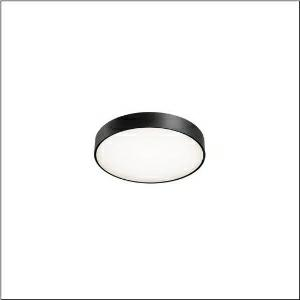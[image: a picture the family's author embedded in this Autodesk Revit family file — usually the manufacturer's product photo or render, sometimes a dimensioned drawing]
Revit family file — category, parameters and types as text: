
# Revit family: round_21_s_51mr34fd0421b
name_source: partatom
category: Lighting Fixtures
units: mm (PartAtom-declared; Revit-internal decimal feet)

## family parameters
Cut with Voids When Loaded = No
Host = Face
Light Source = No
Part Type = Normal
Room Calculation Point = No
Round Connector Dimension = Use Diameter
Shared = No

## types (1)
- Round 21 S (1 x LED, 3910 lm, 30.3 W, 4000K)
    Apparent Load = 30 VA
    CIE Flux Codes = 49 80 96 100 100
    Color Rendering = 80
    Color Temperature = 4000K
    Default Elevation = 1800 mm
    Description = Round 21 S, wall and ceiling luminaire, primary optical cover: cover, of PMMA, opal, light emission: direct distribution, primary light characteristic: symmetric, installation type: suspended mounting, surface-mounted, LED, rated luminous flux: 3.900lm, luminous efficacy: 129lm/W, light colour: 840, colour temperature: 4000K, control gear: DALI 2, with terminal, 5-pole, mains connection: 230V, AC, 50/60Hz, rated input power: 30.3W, housing, of aluminium, coated, black, diameter: 400mm, height: 62mm, protection rating (complete): IP40, insulation class (complete): insulation class I (protective earthing), certification: CE, impact resistance: IK04, permissible operating ambient temperature: -10..+35°C, packaging unit: 1 piece
    Height = 87 mm
    Lamp = 1 x LED
    Lamp Light Flux = 3910 lm
    Lamp Power = 30.3 W
    Lamp count = 1
    Length = 400 mm
    Luminous efficacy = 129 lm/W
    Manufacturer = Siteco
    ModVariant = No
    Model = 51MR34FD0421B
    Mounting Place = Ceiling
    Mounting Type = Surface mounted
    Number of Poles = 1
    OnlyDefault = Yes
    Power Factor = 1
    Product Name = Round 21 S
    Product group = wall and ceiling luminaire | ceiling mounted
    ProductGroupID = 304
    Protection Class = Protection class I
    Protection Degree = IP 40
    RLX_Detail_Level = 1
    RLX_Emergency_Light_Flux = 0 lm
    RLX_Emergency_Type = 0
    RLX_Emergency_Type_DB = No
    RlxData = <blob elided: 13461 chars, md5=f7c21060>
    Socket = socket
    Standby Power = 0 W
    System Light Flux = 3910 lm
    System Power = 30 W
    Type Comments = Product without accessories
    Type Image = l_1258311.jpg
    URL = http://relux.com
    VarID = ---
    Voltage = 0 V
    Weight = 0.00 kg
    Width = 0 mm  [stored 0 ft]

note: [stored X ft] marks values corroborated as IEEE doubles in the binary element streams (Revit-internal decimal feet)

## geometry (parser evidence)
native form markers: Sweep x9
no freeform markers — native parametric forms only
